# Revit family: K4 Tray
name_source: partatom
category: Plumbing Fixtures
units: mm (PartAtom-declared; Revit-internal decimal feet)

## family parameters
Always vertical = Yes
Cut with Voids When Loaded = No
OmniClass Number = 23.45.00.00
OmniClass Title = Sanitary, Laundry, and Cleaning Equipment
Part Type = Normal
Room Calculation Point = No
Round Connector Dimension = Use Diameter
Shared = No
Work Plane-Based = No

## types (1)
- Shower Tray
    Assembly = Pressed
    Brand = Mercer
    Default Elevation = 0 mm  [stored 0 ft]
    Description = NZ Made Shower Tray for KOHC
    Finish = Classic
    Includes = Polybase
    Manufacturer = Mercer
    Material = 1.2mm 304 Stainless Steel
    Model = K Series
    Outlet Material = StainlessSteel
    Outlet options = Bottom, facing North, facing South, facing East, facing West
    Tray Material = StainlessSteel
    Waste = Welded in 50mm outlet

note: [stored X ft] marks values corroborated as IEEE doubles in the binary element streams (Revit-internal decimal feet)

## geometry (parser evidence)
native form markers: Sweep x7
no freeform markers — native parametric forms only
